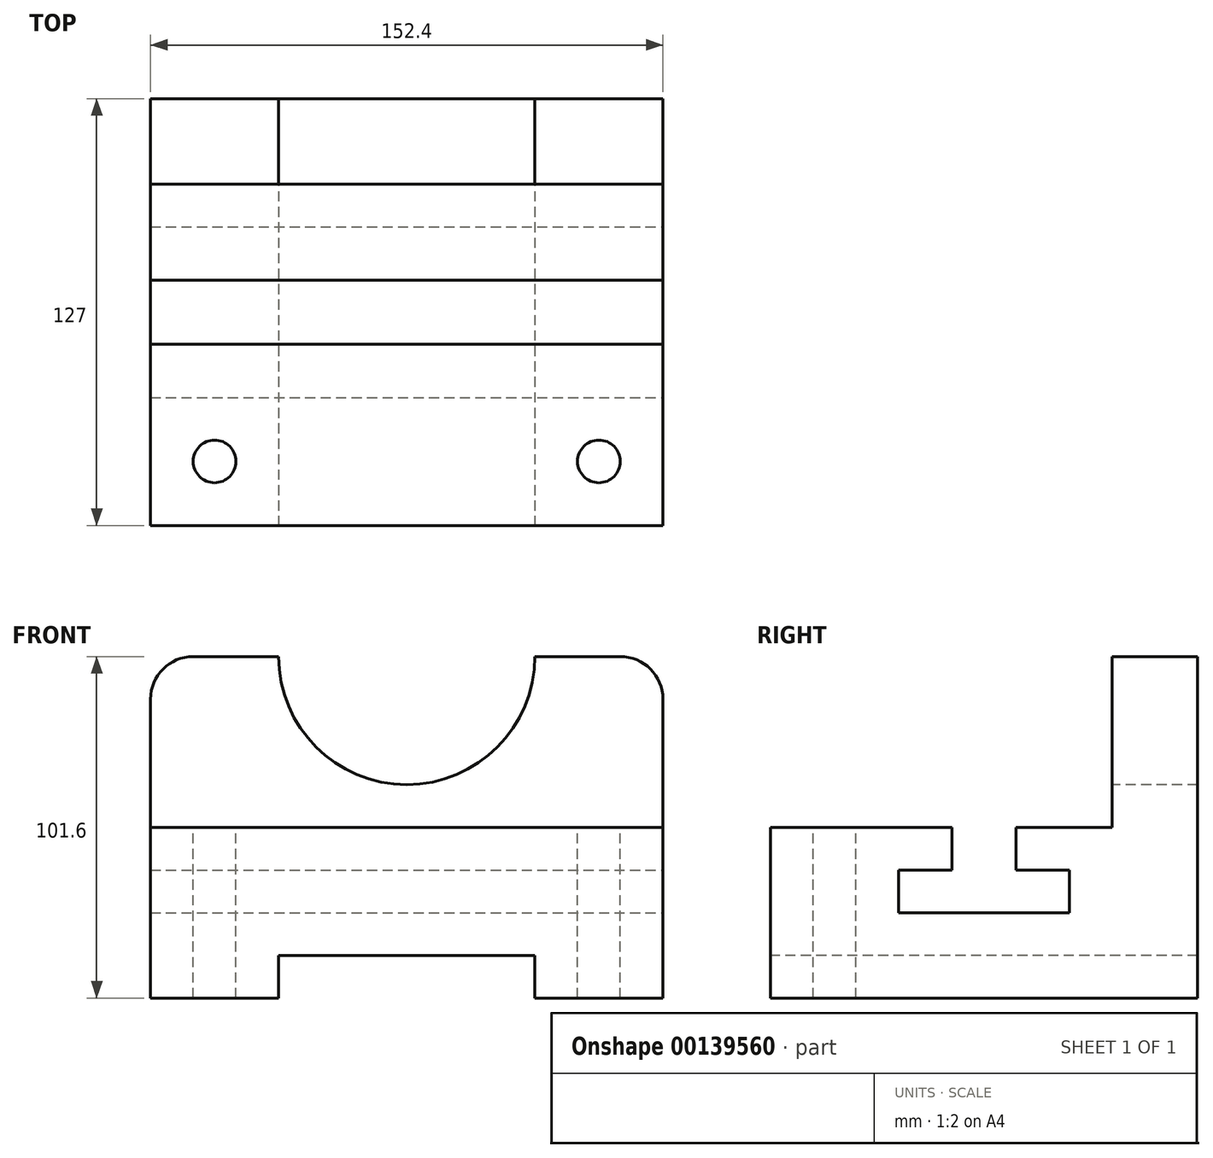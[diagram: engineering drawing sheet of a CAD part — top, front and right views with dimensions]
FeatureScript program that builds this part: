
annotation { "Feature Type Name" : "Feature", "Feature Type Description" : "" }
export const myFeature = defineFeature(function(context is Context, id is Id, definition is map)
    precondition{}
    {
        {
            var Q0;
            Q0=qCreatedBy(makeId("Front.planeOp"),FACE);
            var sketch = newSketch(context, id + "F0", { "sketchPlane" : qUnion([Q0])});
            skLineSegment(sketch, "E0", {"start": v(0, 0) * mm, "end": v(152.4, 0) * mm});
            skLineSegment(sketch, "E1", {"start": v(152.4, 0) * mm, "end": v(152.4, 101.6) * mm});
            skLineSegment(sketch, "E2", {"start": v(152.4, 101.6) * mm, "end": v(0, 101.6) * mm});
            skLineSegment(sketch, "E3", {"start": v(0, 101.6) * mm, "end": v(0, 0) * mm});
            skSolve(sketch);
        }
        {
            var Q0;
            Q0 = qSketchRegion(id + "F0", true);
            extrude(context, id + "F1", {"entities" : qUnion([Q0]), "depth" : 127 * mm});
        }
        {
            var Q0;
            Q0=makeQuery(id+"F1.opExtrude","CAP_FACE",FACE,{"disambiguationData":[OSD([sQuery(id+"F0.wireOp",EDGE,"E0"),sQuery(id+"F0.wireOp",EDGE,"E1"),sQuery(id+"F0.wireOp",EDGE,"E2"),sQuery(id+"F0.wireOp",EDGE,"E3")])],"isStart":false});
            var sketch = newSketch(context, id + "F2", { "sketchPlane" : qUnion([Q0])});
            skLineSegment(sketch, "E4", {"start": v(0, 101.6) * mm, "end": v(0, 50.8) * mm});
            skLineSegment(sketch, "E5", {"start": v(0, 50.8) * mm, "end": v(152.4, 50.8) * mm});
            skLineSegment(sketch, "E6", {"start": v(152.4, 50.8) * mm, "end": v(152.4, 101.6) * mm});
            skLineSegment(sketch, "E7", {"start": v(152.4, 101.6) * mm, "end": v(0, 101.6) * mm});
            skSolve(sketch);
        }
        {
            var Q0;
            Q0 = qSketchRegion(id + "F2", true);
            extrude(context, id + "F3", {"entities" : qUnion([Q0]), "operationType" : NewBodyOperationType.REMOVE, "oppositeDirection" : true, "depth" : 101.6 * mm});
        }
        {
            var Q0;
            Q0=makeQuery(id+"F3.boolean.opBoolean","COPY",FACE,{"derivedFrom":makeQuery(id+"F3.opExtrude","CAP_FACE",FACE,{"disambiguationData":[OSD([sQuery(id+"F2.wireOp",EDGE,"E4"),sQuery(id+"F2.wireOp",EDGE,"E5"),sQuery(id+"F2.wireOp",EDGE,"E6"),sQuery(id+"F2.wireOp",EDGE,"E7")])],"isStart":false})});
            var sketch = newSketch(context, id + "F4", { "sketchPlane" : qUnion([Q0])});
            skArc(sketch, "E8", {"start": v(38.1, 101.6) * mm, "mid": v(76.2, 63.5) * mm, "end": v(114.3, 101.6) * mm});
            skLineSegment(sketch, "E9", {"start": v(38.1, 101.6) * mm, "end": v(114.3, 101.6) * mm});
            skSolve(sketch);
        }
        {
            var Q0;
            Q0 = qSketchRegion(id + "F4", true);
            extrude(context, id + "F5", {"entities" : qUnion([Q0]), "operationType" : NewBodyOperationType.REMOVE, "oppositeDirection" : true, "depth" : 25.4 * mm});
        }
        {
            var Q0;
            Q0=makeQuery(id+"F1.opExtrude","CAP_FACE",FACE,{"disambiguationData":[OSD([sQuery(id+"F0.wireOp",EDGE,"E0"),sQuery(id+"F0.wireOp",EDGE,"E1"),sQuery(id+"F0.wireOp",EDGE,"E2"),sQuery(id+"F0.wireOp",EDGE,"E3")])],"isStart":false});
            var sketch = newSketch(context, id + "F6", { "sketchPlane" : qUnion([Q0])});
            skLineSegment(sketch, "E10", {"start": v(38.1, 0) * mm, "end": v(114.3, 0) * mm});
            skLineSegment(sketch, "E11", {"start": v(114.3, 0) * mm, "end": v(114.3, 12.7) * mm});
            skLineSegment(sketch, "E12", {"start": v(114.3, 12.7) * mm, "end": v(38.1, 12.7) * mm});
            skLineSegment(sketch, "E13", {"start": v(38.1, 12.7) * mm, "end": v(38.1, 0) * mm});
            skSolve(sketch);
        }
        {
            var Q0;
            Q0 = qSketchRegion(id + "F6", true);
            extrude(context, id + "F7", {"entities" : qUnion([Q0]), "operationType" : NewBodyOperationType.REMOVE, "endBound" : BoundingType.THROUGH_ALL, "oppositeDirection" : true, "depth" : 25.4 * mm});
        }
        {
            var Q0;
            Q0=makeQuery(id+"F1.opExtrude","SWEPT_FACE",FACE,{"disambiguationData":[OSD([sQuery(id+"F0.wireOp",EDGE,"E1")])]});
            var sketch = newSketch(context, id + "F8", { "sketchPlane" : qUnion([Q0])});
            skLineSegment(sketch, "E14", {"start": v(-73.03, 50.8) * mm, "end": v(-53.98, 50.8) * mm});
            skLineSegment(sketch, "E15", {"start": v(-53.98, 50.8) * mm, "end": v(-53.98, 38.1) * mm});
            skLineSegment(sketch, "E16", {"start": v(-53.98, 38.1) * mm, "end": v(-38.1, 38.1) * mm});
            skLineSegment(sketch, "E17", {"start": v(-38.1, 38.1) * mm, "end": v(-38.1, 25.4) * mm});
            skLineSegment(sketch, "E18", {"start": v(-38.1, 25.4) * mm, "end": v(-88.9, 25.4) * mm});
            skLineSegment(sketch, "E19", {"start": v(-88.9, 25.4) * mm, "end": v(-88.9, 38.1) * mm});
            skLineSegment(sketch, "E20", {"start": v(-88.9, 38.1) * mm, "end": v(-73.03, 38.1) * mm});
            skLineSegment(sketch, "E21", {"start": v(-73.03, 38.1) * mm, "end": v(-73.03, 50.8) * mm});
            skSolve(sketch);
        }
        {
            var Q0;
            Q0 = qSketchRegion(id + "F8", true);
            extrude(context, id + "F9", {"entities" : qUnion([Q0]), "operationType" : NewBodyOperationType.REMOVE, "endBound" : BoundingType.THROUGH_ALL, "oppositeDirection" : true, "depth" : 25.4 * mm});
        }
        {
            var Q0;
            Q0=makeQuery(id+"F9.boolean.opBoolean","SPLIT",FACE,{"disambiguationData":[TD([makeQuery(id+"F9.opExtrude","SWEPT_FACE",FACE,{"disambiguationData":[OSD([sQuery(id+"F8.wireOp",EDGE,"E21")])]})])],"derivedFrom":makeQuery(id+"F3.boolean.opBoolean","COPY",FACE,{"derivedFrom":makeQuery(id+"F3.opExtrude","SWEPT_FACE",FACE,{"disambiguationData":[OSD([sQuery(id+"F2.wireOp",EDGE,"E5")])]})})});
            var sketch = newSketch(context, id + "F10", { "sketchPlane" : qUnion([Q0])});
            skCircle(sketch, "E22", {"center": v(19.05, -107.95) * mm, "radius": 6.35 * mm});
            skLineSegment(sketch, "E23", {"start": v(76.2, -127) * mm, "end": v(76.2, -73.02) * mm, "construction": true});
            skPoint(sketch, "E24", {"position": v(76.2, -73.02) * mm});
            skCircle(sketch, "E25.MirrorC", {"center": v(133.35, -107.95) * mm, "radius": 6.35 * mm});
            skSolve(sketch);
        }
        {
            var Q0;
            Q0 = qSketchRegion(id + "F10", true);
            extrude(context, id + "F11", {"entities" : qUnion([Q0]), "operationType" : NewBodyOperationType.REMOVE, "endBound" : BoundingType.THROUGH_ALL, "oppositeDirection" : true, "depth" : 25.4 * mm});
        }
        {
            var Q0;
            Q0=makeQuery(id+"F1.opExtrude","SWEPT_EDGE",EDGE,{"disambiguationData":[OSD([sQuery(id+"F0.wireOp",EDGE,"E1"),sQuery(id+"F0.wireOp",EDGE,"E2")])]});
            var Q1;
            Q1=makeQuery(id+"F1.opExtrude","SWEPT_EDGE",EDGE,{"disambiguationData":[OSD([sQuery(id+"F0.wireOp",EDGE,"E2"),sQuery(id+"F0.wireOp",EDGE,"E3")])]});
            fillet(context, id + "F12", {"entities" : qUnion([Q0, Q1]), "radius" : 12.7 * mm, "tangentPropagation" : true, "allowEdgeOverflow" : false});
        }
    });
